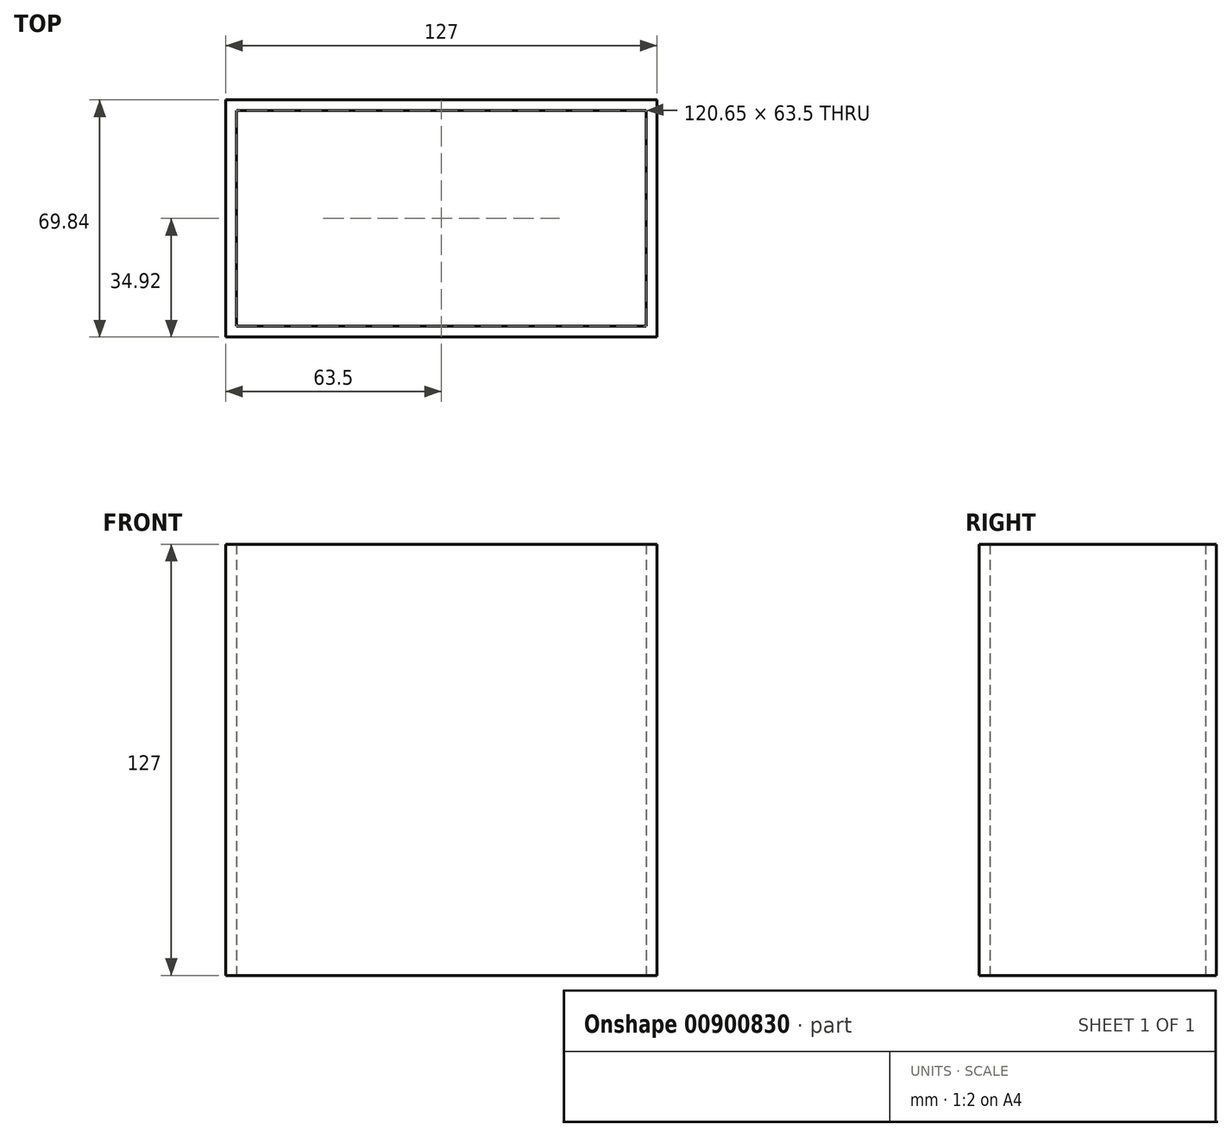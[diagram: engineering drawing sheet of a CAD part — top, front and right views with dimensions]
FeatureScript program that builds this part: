
annotation { "Feature Type Name" : "Feature", "Feature Type Description" : "" }
export const myFeature = defineFeature(function(context is Context, id is Id, definition is map)
    precondition{}
    {
        {
            var Q0;
            Q0=qCreatedBy(makeId("Top.planeOp"),FACE);
            var sketch = newSketch(context, id + "F0", { "sketchPlane" : qUnion([Q0])});
            skLineSegment(sketch, "E0.bottom", {"start": v(-63.5, 34.93) * mm, "end": v(63.5, 34.93) * mm});
            skLineSegment(sketch, "E0.top", {"start": v(-63.5, -34.93) * mm, "end": v(63.5, -34.93) * mm});
            skLineSegment(sketch, "E0.left", {"start": v(-63.5, 34.93) * mm, "end": v(-63.5, -34.93) * mm});
            skLineSegment(sketch, "E0.right", {"start": v(63.5, 34.93) * mm, "end": v(63.5, -34.93) * mm});
            skLineSegment(sketch, "E1.bottom", {"start": v(-60.33, 31.75) * mm, "end": v(60.33, 31.75) * mm});
            skLineSegment(sketch, "E1.top", {"start": v(-60.33, -31.75) * mm, "end": v(60.33, -31.75) * mm});
            skLineSegment(sketch, "E1.left", {"start": v(-60.33, 31.75) * mm, "end": v(-60.33, -31.75) * mm});
            skLineSegment(sketch, "E1.right", {"start": v(60.33, 31.75) * mm, "end": v(60.33, -31.75) * mm});
            skSolve(sketch);
        }
        {
            var Q0;
            Q0 = qSketchRegion(id + "F0", true);
            extrude(context, id + "F1", {"entities" : qUnion([Q0]), "depth" : 127 * mm, "offsetDistance" : 25.4 * mm});
        }
        {
            var Q0;
            Q0=qCreatedBy(makeId("Right.planeOp"),FACE);
            var sketch = newSketch(context, id + "F2", { "sketchPlane" : qUnion([Q0])});
            skCircle(sketch, "E2", {"center": v(-17.67, 52.95) * mm, "radius": 6.82 * mm});
            skSolve(sketch);
        }
        {
            var Q0;
            Q0 = qSketchRegion(id + "F2", true);
            extrude(context, id + "F3", {"entities" : qUnion([Q0]), "operationType" : NewBodyOperationType.REMOVE, "oppositeDirection" : true, "depth" : 25.4 * mm, "offsetDistance" : 25.4 * mm});
        }
    });
